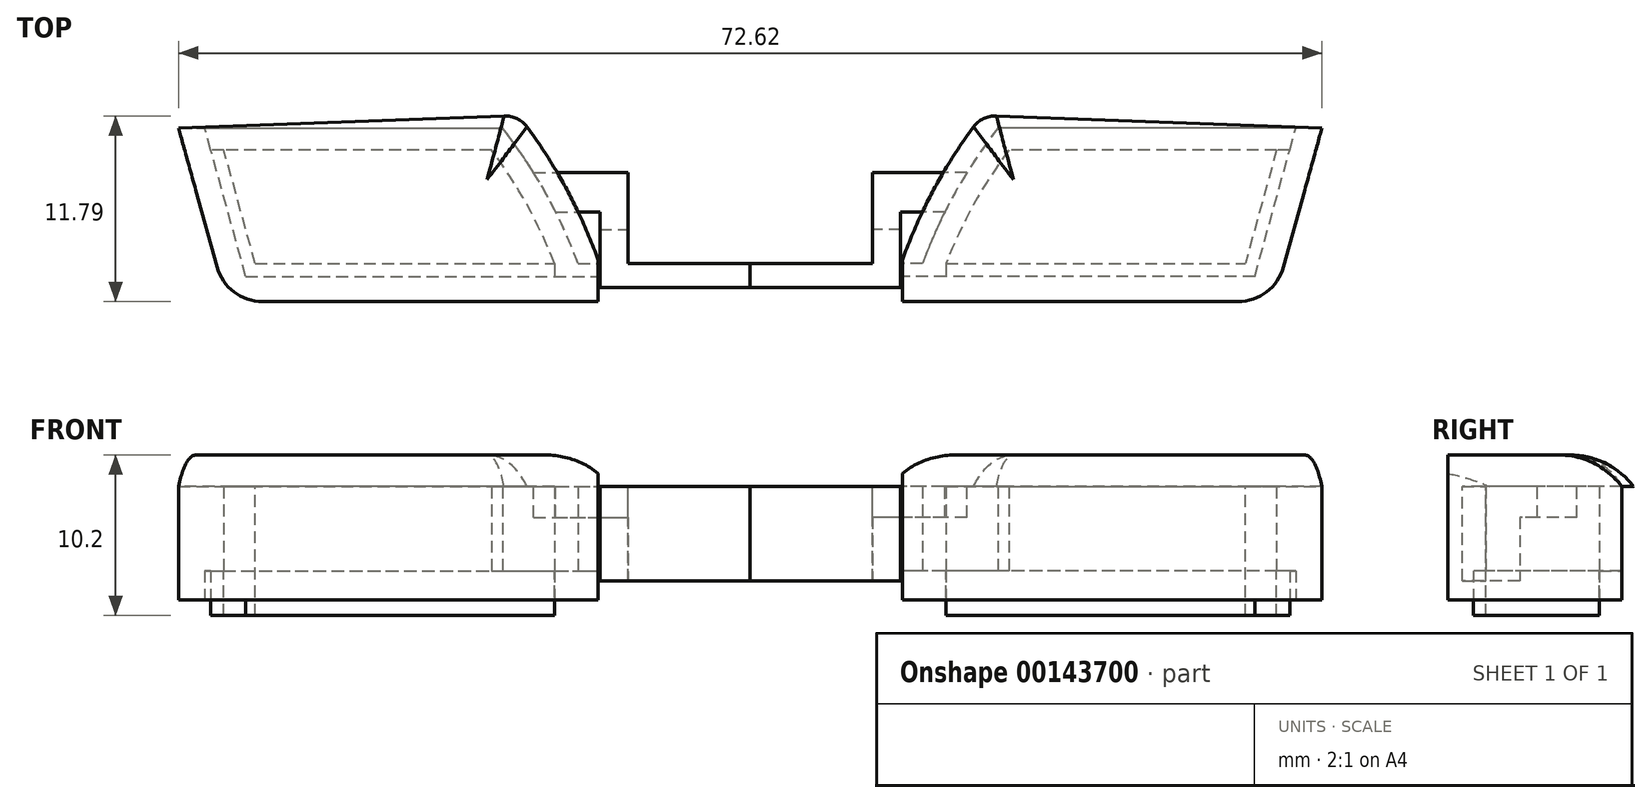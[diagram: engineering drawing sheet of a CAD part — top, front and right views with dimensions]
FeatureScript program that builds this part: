
annotation { "Feature Type Name" : "Feature", "Feature Type Description" : "" }
export const myFeature = defineFeature(function(context is Context, id is Id, definition is map)
    precondition{}
    {
        {
            var Q0;
            Q0=qCreatedBy(makeId("Top.planeOp"),FACE);
            var sketch = newSketch(context, id + "F0", { "sketchPlane" : qUnion([Q0])});
            skLineSegment(sketch, "E0", {"start": v(0, 0) * mm, "end": v(-19, 0) * mm});
            skLineSegment(sketch, "E1", {"start": v(0, 0) * mm, "end": v(2, 7.23) * mm});
            skLineSegment(sketch, "E2", {"start": v(2, 7.23) * mm, "end": v(-15, 7.23) * mm});
            skArc(sketch, "E3", {"start": v(-15, 7.23) * mm, "mid": v(-17.25, 3.75) * mm, "end": v(-19, 0) * mm});
            skLineSegment(sketch, "E4", {"start": v(0, 0) * mm, "end": v(0, 7.23) * mm, "construction": true});
            skLineSegment(sketch, "E5.0", {"start": v(1.83, -2.4) * mm, "end": v(-19, -2.4) * mm});
            skLineSegment(sketch, "E5.1", {"start": v(1.83, -2.4) * mm, "end": v(4.5, 7.23) * mm});
            skArc(sketch, "E6.0", {"start": v(-15.7, 8.63) * mm, "mid": v(-18.64, 4.13) * mm, "end": v(-20.78, -0.8) * mm});
            skLineSegment(sketch, "E6.1", {"start": v(2.59, 8.63) * mm, "end": v(-15.7, 8.63) * mm});
            skLineSegment(sketch, "E7", {"start": v(-19, 0) * mm, "end": v(-23.59, 0) * mm, "construction": true});
            skLineSegment(sketch, "E8", {"start": v(4.5, 7.23) * mm, "end": v(4.88, 8.63) * mm});
            skLineSegment(sketch, "E9", {"start": v(4.88, 8.63) * mm, "end": v(2.59, 8.63) * mm});
            skLineSegment(sketch, "E10", {"start": v(-19, 0) * mm, "end": v(-21.78, 0) * mm});
            skLineSegment(sketch, "E11", {"start": v(-21.78, 0) * mm, "end": v(-21.78, -2.4) * mm});
            skLineSegment(sketch, "E12", {"start": v(-21.78, -2.4) * mm, "end": v(-19, -2.4) * mm});
            skLineSegment(sketch, "E13.0", {"start": v(0.6, -0.8) * mm, "end": v(-19, -0.8) * mm});
            skLineSegment(sketch, "E13.1", {"start": v(0.6, -0.8) * mm, "end": v(2.83, 7.23) * mm});
            skLineSegment(sketch, "E14", {"start": v(-19, 0) * mm, "end": v(-19, -0.8) * mm});
            skLineSegment(sketch, "E15", {"start": v(-19, -0.8) * mm, "end": v(-21.78, -0.8) * mm});
            skLineSegment(sketch, "E16", {"start": v(2, 7.23) * mm, "end": v(4.5, 7.23) * mm, "construction": true});
            skLineSegment(sketch, "E17", {"start": v(2, 7.23) * mm, "end": v(2.83, 7.23) * mm});
            skLineSegment(sketch, "E18", {"start": v(-19, -0.8) * mm, "end": v(-19, -2.4) * mm});
            skSolve(sketch);
        }
        {
            var Q0;
            Q0=makeQuery(id+"F0.imprint","IMPRINT",FACE,{"disambiguationData":[TD([[makeQuery(id+"F0.imprint","IMPRINT",EDGE,{"derivedFrom":sQuery(id+"F0.wireOp",EDGE,"E2")}),-1.0]])]});
            var Q1;
            Q1=makeQuery(id+"F0.imprint","IMPRINT",FACE,{"disambiguationData":[TD([[makeQuery(id+"F0.imprint","IMPRINT",EDGE,{"derivedFrom":sQuery(id+"F0.wireOp",EDGE,"E0")}),-1.0]])]});
            var Q2;
            Q2=makeQuery(id+"F0.imprint","IMPRINT",FACE,{"disambiguationData":[TD([[makeQuery(id+"F0.imprint","IMPRINT",EDGE,{"derivedFrom":sQuery(id+"F0.wireOp",EDGE,"E0")}),1.0]])]});
            var Q3;
            {var subQ5=sQuery(id+"F0.wireOp",EDGE,"E14");Q3=makeQuery(id+"F0.imprint","IMPRINT",FACE,{"disambiguationData":[TD([[makeQuery(id+"F0.imprint","IMPRINT",EDGE,{"derivedFrom":subQ5}),-1.0]])]});}
            var Q4;
            {var subQ0=sQuery(id+"F0.wireOp",EDGE,"E15");var subQ1=sQuery(id+"F0.wireOp",EDGE,"E6.0");var subQ2=makeQuery(id+"F0.imprint","INTERSECT",VERTEX,{"derivedFrom":[subQ1,subQ0]});Q4=makeQuery(id+"F0.imprint","IMPRINT",FACE,{"disambiguationData":[TD([[makeQuery(id+"F0.imprint","IMPRINT",EDGE,{"disambiguationData":[TD([[subQ2,1.0]])],"derivedFrom":subQ1}),-1.0]])]});}
            var Q5;
            {var subQ5=sQuery(id+"F0.wireOp",EDGE,"E12");Q5=makeQuery(id+"F0.imprint","IMPRINT",FACE,{"disambiguationData":[TD([[makeQuery(id+"F0.imprint","IMPRINT",EDGE,{"derivedFrom":subQ5}),1.0]])]});}
            extrude(context, id + "F1", {"entities" : qUnion([Q0, Q1, Q2, Q3, Q4, Q5]), "depth" : 7.2 * mm});
        }
        {
            var Q0;
            Q0=makeQuery(id+"F0.imprint","IMPRINT",FACE,{"disambiguationData":[TD([[makeQuery(id+"F0.imprint","IMPRINT",EDGE,{"derivedFrom":sQuery(id+"F0.wireOp",EDGE,"E0")}),1.0]])]});
            extrude(context, id + "F2", {"entities" : qUnion([Q0]), "operationType" : NewBodyOperationType.ADD, "oppositeDirection" : true, "depth" : 1 * mm});
        }
        {
            var Q0;
            Q0=makeQuery(id+"F0.imprint","IMPRINT",FACE,{"disambiguationData":[TD([[makeQuery(id+"F0.imprint","IMPRINT",EDGE,{"derivedFrom":sQuery(id+"F0.wireOp",EDGE,"E0")}),-1.0]])]});
            extrude(context, id + "F3", {"entities" : qUnion([Q0]), "operationType" : NewBodyOperationType.REMOVE, "depth" : 7.25 * mm});
        }
        {
            var Q0;
            Q0=makeQuery(id+"F1.opExtrude","CAP_FACE",FACE,{"disambiguationData":[OSD([sQuery(id+"F0.wireOp",EDGE,"E5.0"),sQuery(id+"F0.wireOp",EDGE,"E5.1"),sQuery(id+"F0.wireOp",EDGE,"E6.0"),sQuery(id+"F0.wireOp",EDGE,"E6.1"),sQuery(id+"F0.wireOp",EDGE,"E8"),sQuery(id+"F0.wireOp",EDGE,"E9"),sQuery(id+"F0.wireOp",EDGE,"E10"),sQuery(id+"F0.wireOp",EDGE,"E11"),sQuery(id+"F0.wireOp",EDGE,"E12")])],"isStart":true});
            var sketch = newSketch(context, id + "F4", { "sketchPlane" : qUnion([Q0])});
            skLineSegment(sketch, "E19.0", {"start": v(2, -7.23) * mm, "end": v(-15, -7.23) * mm});
            skLineSegment(sketch, "E20.0", {"start": v(4.88, -8.63) * mm, "end": v(-15.7, -8.63) * mm});
            skArc(sketch, "E21.0", {"start": v(-15.7, -8.63) * mm, "mid": v(-18.43, -4.5) * mm, "end": v(-20.5, 0) * mm});
            skArc(sketch, "E22.0", {"start": v(-15, -7.23) * mm, "mid": v(-17.25, -3.75) * mm, "end": v(-19, 0) * mm});
            skLineSegment(sketch, "E23", {"start": v(-19, 0.8) * mm, "end": v(-20.5, 0.8) * mm});
            skLineSegment(sketch, "E24", {"start": v(-20.5, 0.8) * mm, "end": v(-20.5, 0) * mm});
            skLineSegment(sketch, "E25.0", {"start": v(0, 0) * mm, "end": v(2, -7.23) * mm});
            skLineSegment(sketch, "E26", {"start": v(2, -7.23) * mm, "end": v(2.39, -8.63) * mm});
            skLineSegment(sketch, "E27", {"start": v(-20.5, 0.8) * mm, "end": v(-21.78, 0.8) * mm});
            skLineSegment(sketch, "E28", {"start": v(-21.78, 0.8) * mm, "end": v(-21.78, 0) * mm});
            skLineSegment(sketch, "E29", {"start": v(-21.78, 0) * mm, "end": v(-20.5, 0) * mm});
            skLineSegment(sketch, "E30.0", {"start": v(2, -7.23) * mm, "end": v(2.83, -7.23) * mm});
            skLineSegment(sketch, "E31.0", {"start": v(0.6, 0.8) * mm, "end": v(2.83, -7.23) * mm});
            skLineSegment(sketch, "E32", {"start": v(2.83, -7.23) * mm, "end": v(3.22, -8.63) * mm});
            skSolve(sketch);
        }
        {
            var Q0;
            Q0=makeQuery(id+"F4.imprint","IMPRINT",FACE,{"disambiguationData":[TD([[makeQuery(id+"F4.imprint","IMPRINT",EDGE,{"derivedFrom":sQuery(id+"F4.wireOp",EDGE,"E19.0")}),1.0]])]});
            var Q1;
            Q1=makeQuery(id+"F4.imprint","IMPRINT",FACE,{"disambiguationData":[TD([[makeQuery(id+"F4.imprint","IMPRINT",EDGE,{"derivedFrom":sQuery(id+"F4.wireOp",EDGE,"E24")}),-1.0]])]});
            var Q2;
            {var subQ0=sQuery(id+"F4.wireOp",EDGE,"E26");Q2=makeQuery(id+"F4.imprint","IMPRINT",FACE,{"disambiguationData":[TD([[makeQuery(id+"F4.imprint","IMPRINT",EDGE,{"derivedFrom":subQ0}),1.0]])]});}
            extrude(context, id + "F5", {"entities" : qUnion([Q0, Q1, Q2]), "operationType" : NewBodyOperationType.REMOVE, "oppositeDirection" : true, "depth" : 1.85 * mm});
        }
        {
            var Q0;
            Q0=makeQuery(id+"F1.opExtrude","CAP_FACE",FACE,{"disambiguationData":[OSD([sQuery(id+"F0.wireOp",EDGE,"E5.0"),sQuery(id+"F0.wireOp",EDGE,"E5.1"),sQuery(id+"F0.wireOp",EDGE,"E6.0"),sQuery(id+"F0.wireOp",EDGE,"E6.1"),sQuery(id+"F0.wireOp",EDGE,"E8"),sQuery(id+"F0.wireOp",EDGE,"E9"),sQuery(id+"F0.wireOp",EDGE,"E10"),sQuery(id+"F0.wireOp",EDGE,"E11"),sQuery(id+"F0.wireOp",EDGE,"E12")])],"isStart":false});
            var sketch = newSketch(context, id + "F6", { "sketchPlane" : qUnion([Q0])});
            skArc(sketch, "E33.0", {"start": v(-17.25, 8.69) * mm, "mid": v(-19.83, 4.62) * mm, "end": v(-21.78, 0.22) * mm});
            skLineSegment(sketch, "E34", {"start": v(-21.78, 0.22) * mm, "end": v(-21.78, 0) * mm});
            skLineSegment(sketch, "E35", {"start": v(-15.8, 9.39) * mm, "end": v(4.88, 8.63) * mm});
            skPoint(sketch, "E36.visualSharp", {"position": v(-16.7, 9.42) * mm});
            skArc(sketch, "E36.filletArc", {"start": v(-15.8, 9.39) * mm, "mid": v(-16.61, 9.22) * mm, "end": v(-17.25, 8.69) * mm});
            skLineSegment(sketch, "E37.0", {"start": v(1.83, -2.4) * mm, "end": v(4.88, 8.63) * mm});
            skLineSegment(sketch, "E38.0", {"start": v(1.83, -2.4) * mm, "end": v(-21.78, -2.4) * mm});
            skLineSegment(sketch, "E39.0", {"start": v(-21.78, 0) * mm, "end": v(-21.78, -2.4) * mm});
            skArc(sketch, "E40.0", {"start": v(-19, 0) * mm, "mid": v(-17.25, 3.75) * mm, "end": v(-15, 7.23) * mm});
            skLineSegment(sketch, "E41.0", {"start": v(-19, 0) * mm, "end": v(0, 0) * mm});
            skLineSegment(sketch, "E42.0", {"start": v(2, 7.23) * mm, "end": v(0, 0) * mm});
            skLineSegment(sketch, "E43.0", {"start": v(-15, 7.23) * mm, "end": v(2, 7.23) * mm});
            skSolve(sketch);
        }
        {
            var Q0;
            Q0=makeQuery(id+"F6.imprint","IMPRINT",FACE,{"disambiguationData":[TD([[makeQuery(id+"F6.imprint","IMPRINT",EDGE,{"derivedFrom":sQuery(id+"F6.wireOp",EDGE,"E40.0")}),-1.0]])]});
            var Q1;
            Q1=makeQuery(id+"F6.imprint","IMPRINT",FACE,{"disambiguationData":[TD([[makeQuery(id+"F6.imprint","IMPRINT",EDGE,{"derivedFrom":sQuery(id+"F6.wireOp",EDGE,"E37.0")}),1.0]])]});
            var Q2;
            Q2=makeQuery(id+"F6.imprint","IMPRINT",FACE,{"disambiguationData":[TD([[makeQuery(id+"F6.imprint","IMPRINT",EDGE,{"derivedFrom":sQuery(id+"F6.wireOp",EDGE,"E33.0")}),1.0]])]});
            extrude(context, id + "F7", {"entities" : qUnion([Q0, Q1, Q2]), "operationType" : NewBodyOperationType.ADD, "depth" : 2 * mm});
        }
        {
            var Q0;
            Q0=makeQuery(id+"F7.opExtrude","CAP_EDGE",EDGE,{"disambiguationData":[OSD([sQuery(id+"F6.wireOp",EDGE,"E33.0")])],"isStart":false});
            var Q1;
            Q1=makeQuery(id+"F7.opExtrude","CAP_EDGE",EDGE,{"disambiguationData":[OSD([sQuery(id+"F6.wireOp",EDGE,"E36.filletArc")])],"isStart":false});
            var Q2;
            Q2=makeQuery(id+"F7.opExtrude","CAP_EDGE",EDGE,{"disambiguationData":[OSD([sQuery(id+"F6.wireOp",EDGE,"E35")])],"isStart":false});
            fillet(context, id + "F8", {"entities" : qUnion([Q0, Q1, Q2]), "radius" : 5 * mm, "tangentPropagation" : true, "allowEdgeOverflow" : false});
        }
        {
            var Q0;
            {var subQ0=sQuery(id+"F6.wireOp",EDGE,"E39.0");var subQ1=sQuery(id+"F6.wireOp",EDGE,"E34");var subQ2=sQuery(id+"F6.wireOp",EDGE,"E33.0");var subQ3=sQuery(id+"F6.wireOp",EDGE,"E35");var subQ4=sQuery(id+"F6.wireOp",EDGE,"E36.filletArc");var subQ5=sQuery(id+"F6.wireOp",EDGE,"E37.0");Q0=makeQuery(id+"F7.boolean.opBoolean","SPLIT",FACE,{"disambiguationData":[TD([makeQuery(id+"F1.opExtrude","SWEPT_FACE",FACE,{"disambiguationData":[OSD([sQuery(id+"F0.wireOp",EDGE,"E6.0")])]})])],"derivedFrom":makeQuery(id+"F7.opExtrude","CAP_FACE",FACE,{"disambiguationData":[OSD([subQ2,subQ1,subQ3,subQ4,subQ5,sQuery(id+"F6.wireOp",EDGE,"E38.0"),subQ0])],"isStart":true})});}
            var sketch = newSketch(context, id + "F9", { "sketchPlane" : qUnion([Q0])});
            skLineSegment(sketch, "E44.0", {"start": v(1.83, 2.4) * mm, "end": v(-21.78, 2.4) * mm});
            skArc(sketch, "E45.0", {"start": v(-15.7, -8.63) * mm, "mid": v(-18.43, -4.5) * mm, "end": v(-20.5, 0) * mm});
            skPoint(sketch, "E46", {"position": v(-17.68, -5.78) * mm});
            skLineSegment(sketch, "E47", {"start": v(-17.68, -5.78) * mm, "end": v(-23.68, -5.78) * mm});
            skLineSegment(sketch, "E48", {"start": v(-23.68, -5.78) * mm, "end": v(-23.68, -2.98) * mm});
            skLineSegment(sketch, "E49", {"start": v(-23.68, -2.98) * mm, "end": v(-23.68, 0) * mm});
            skLineSegment(sketch, "E50", {"start": v(-23.68, 0) * mm, "end": v(-31.43, 0) * mm});
            skLineSegment(sketch, "E51.0", {"start": v(-19.08, -3.28) * mm, "end": v(-23.68, -3.28) * mm});
            skLineSegment(sketch, "E52.0", {"start": v(-21.88, -2.98) * mm, "end": v(-21.88, 0) * mm});
            skLineSegment(sketch, "E52.1", {"start": v(-21.88, -5.78) * mm, "end": v(-21.88, -2.98) * mm});
            skLineSegment(sketch, "E53.0", {"start": v(-23.68, 1.5) * mm, "end": v(-31.43, 1.5) * mm});
            skLineSegment(sketch, "E54", {"start": v(-23.68, 1.5) * mm, "end": v(-21.88, 1.5) * mm});
            skLineSegment(sketch, "E55", {"start": v(-21.88, 1.5) * mm, "end": v(-21.88, 0) * mm});
            skLineSegment(sketch, "E56", {"start": v(-31.43, 1.5) * mm, "end": v(-31.43, 0) * mm});
            skSolve(sketch);
        }
        {
            var Q0;
            {var subQ5=sQuery(id+"F9.wireOp",EDGE,"E49");Q0=makeQuery(id+"F9.imprint","IMPRINT",FACE,{"disambiguationData":[TD([[makeQuery(id+"F9.imprint","IMPRINT",EDGE,{"derivedFrom":subQ5}),-1.0]])]});}
            var Q1;
            {var subQ0=sQuery(id+"F9.wireOp",EDGE,"E48");var subQ1=sQuery(id+"F9.wireOp",EDGE,"E47");var subQ2=makeQuery(id+"F9.imprint","INTERSECT",VERTEX,{"derivedFrom":[subQ1,subQ0]});Q1=makeQuery(id+"F9.imprint","IMPRINT",FACE,{"disambiguationData":[TD([[makeQuery(id+"F9.imprint","IMPRINT",EDGE,{"disambiguationData":[TD([[subQ2,1.0]])],"derivedFrom":subQ1}),-1.0]])]});}
            var Q2;
            {var subQ0=sQuery(id+"F9.wireOp",EDGE,"E52.1");var subQ1=sQuery(id+"F9.wireOp",EDGE,"E47");var subQ2=makeQuery(id+"F9.imprint","INTERSECT",VERTEX,{"derivedFrom":[subQ1,subQ0]});Q2=makeQuery(id+"F9.imprint","IMPRINT",FACE,{"disambiguationData":[TD([[makeQuery(id+"F9.imprint","IMPRINT",EDGE,{"disambiguationData":[TD([[subQ2,-1.0]])],"derivedFrom":subQ0}),-1.0]])]});}
            var Q3;
            {var subQ0=sQuery(id+"F9.wireOp",EDGE,"E47");var subQ1=sQuery(id+"F9.wireOp",EDGE,"E45.0");var subQ2=makeQuery(id+"F9.imprint","INTERSECT",VERTEX,{"derivedFrom":[subQ1,subQ0]});Q3=makeQuery(id+"F9.imprint","IMPRINT",FACE,{"disambiguationData":[TD([[makeQuery(id+"F9.imprint","IMPRINT",EDGE,{"disambiguationData":[TD([[subQ2,-1.0]])],"derivedFrom":subQ1}),1.0]])]});}
            extrude(context, id + "F10", {"entities" : qUnion([Q0, Q1, Q2, Q3]), "operationType" : NewBodyOperationType.ADD, "depth" : 6 * mm});
        }
        {
            var Q0;
            Q0=makeQuery(id+"F10.opExtrude","CAP_FACE",FACE,{"disambiguationData":[OSD([sQuery(id+"F9.wireOp",EDGE,"E45.0"),sQuery(id+"F9.wireOp",EDGE,"E47"),sQuery(id+"F9.wireOp",EDGE,"E48"),sQuery(id+"F9.wireOp",EDGE,"E49"),sQuery(id+"F9.wireOp",EDGE,"E50"),sQuery(id+"F9.wireOp",EDGE,"E51.0"),sQuery(id+"F9.wireOp",EDGE,"E52.0"),sQuery(id+"F9.wireOp",EDGE,"E52.1"),sQuery(id+"F9.wireOp",EDGE,"E53.0"),sQuery(id+"F9.wireOp",EDGE,"E54"),sQuery(id+"F9.wireOp",EDGE,"E55"),sQuery(id+"F9.wireOp",EDGE,"E56")])],"isStart":false});
            var sketch = newSketch(context, id + "F11", { "sketchPlane" : qUnion([Q0])});
            skLineSegment(sketch, "E57.0.0", {"start": v(-23.68, 0) * mm, "end": v(-23.68, -5.78) * mm});
            skLineSegment(sketch, "E57.0.1", {"start": v(-23.68, -5.78) * mm, "end": v(-17.68, -5.78) * mm});
            skArc(sketch, "E57.0.2", {"start": v(-17.68, -5.78) * mm, "mid": v(-18.41, -4.55) * mm, "end": v(-19.08, -3.28) * mm});
            skLineSegment(sketch, "E57.0.3", {"start": v(-19.08, -3.28) * mm, "end": v(-21.88, -3.28) * mm});
            skLineSegment(sketch, "E57.0.4", {"start": v(-21.88, -3.28) * mm, "end": v(-21.88, 1.5) * mm});
            skLineSegment(sketch, "E57.0.5", {"start": v(-21.88, 1.5) * mm, "end": v(-31.43, 1.5) * mm});
            skLineSegment(sketch, "E57.0.6", {"start": v(-31.43, 1.5) * mm, "end": v(-31.43, 0) * mm});
            skLineSegment(sketch, "E57.0.7", {"start": v(-31.43, 0) * mm, "end": v(-23.68, 0) * mm});
            skLineSegment(sketch, "E58", {"start": v(-21.88, -2.17) * mm, "end": v(-23.68, -2.17) * mm});
            skSolve(sketch);
        }
        {
            var Q0;
            {var subQ1=sQuery(id+"F11.wireOp",EDGE,"E57.0.1");Q0=makeQuery(id+"F11.imprint","IMPRINT",FACE,{"disambiguationData":[TD([[makeQuery(id+"F11.imprint","IMPRINT",EDGE,{"derivedFrom":subQ1}),-1.0]])]});}
            extrude(context, id + "F12", {"entities" : qUnion([Q0]), "operationType" : NewBodyOperationType.REMOVE, "oppositeDirection" : true, "depth" : (6 - 1.95) * mm});
        }
        {
            var Q0;
            Q0=makeQuery(id+"F7.boolean.opBoolean","MERGE",EDGE,{"derivedFrom":[makeQuery(id+"F1.opExtrude","SWEPT_EDGE",EDGE,{"disambiguationData":[OSD([sQuery(id+"F0.wireOp",EDGE,"E5.0"),sQuery(id+"F0.wireOp",EDGE,"E5.1")])]}),makeQuery(id+"F7.opExtrude","SWEPT_EDGE",EDGE,{"disambiguationData":[OSD([sQuery(id+"F6.wireOp",EDGE,"E37.0"),sQuery(id+"F6.wireOp",EDGE,"E38.0")])]})]});
            fillet(context, id + "F13", {"entities" : qUnion([Q0]), "radius" : 3 * mm, "tangentPropagation" : true, "allowEdgeOverflow" : false});
        }
        {
            var Q0;
            Q0=makeQuery(id+"F1.opExtrude","SWEPT_BODY",BODY,{"disambiguationData":[OSD([sQuery(id+"F0.wireOp",EDGE,"E5.0"),sQuery(id+"F0.wireOp",EDGE,"E5.1"),sQuery(id+"F0.wireOp",EDGE,"E6.0"),sQuery(id+"F0.wireOp",EDGE,"E6.1"),sQuery(id+"F0.wireOp",EDGE,"E8"),sQuery(id+"F0.wireOp",EDGE,"E9"),sQuery(id+"F0.wireOp",EDGE,"E10"),sQuery(id+"F0.wireOp",EDGE,"E11"),sQuery(id+"F0.wireOp",EDGE,"E12")])]});
            var Q1;
            Q1=makeQuery(id+"F10.opExtrude","SWEPT_FACE",FACE,{"disambiguationData":[OSD([sQuery(id+"F9.wireOp",EDGE,"E56")])]});
            mirror(context, id + "F14", {"entities" : qUnion([Q0]), "mirrorPlane" : qUnion([Q1])});
        }
    });
